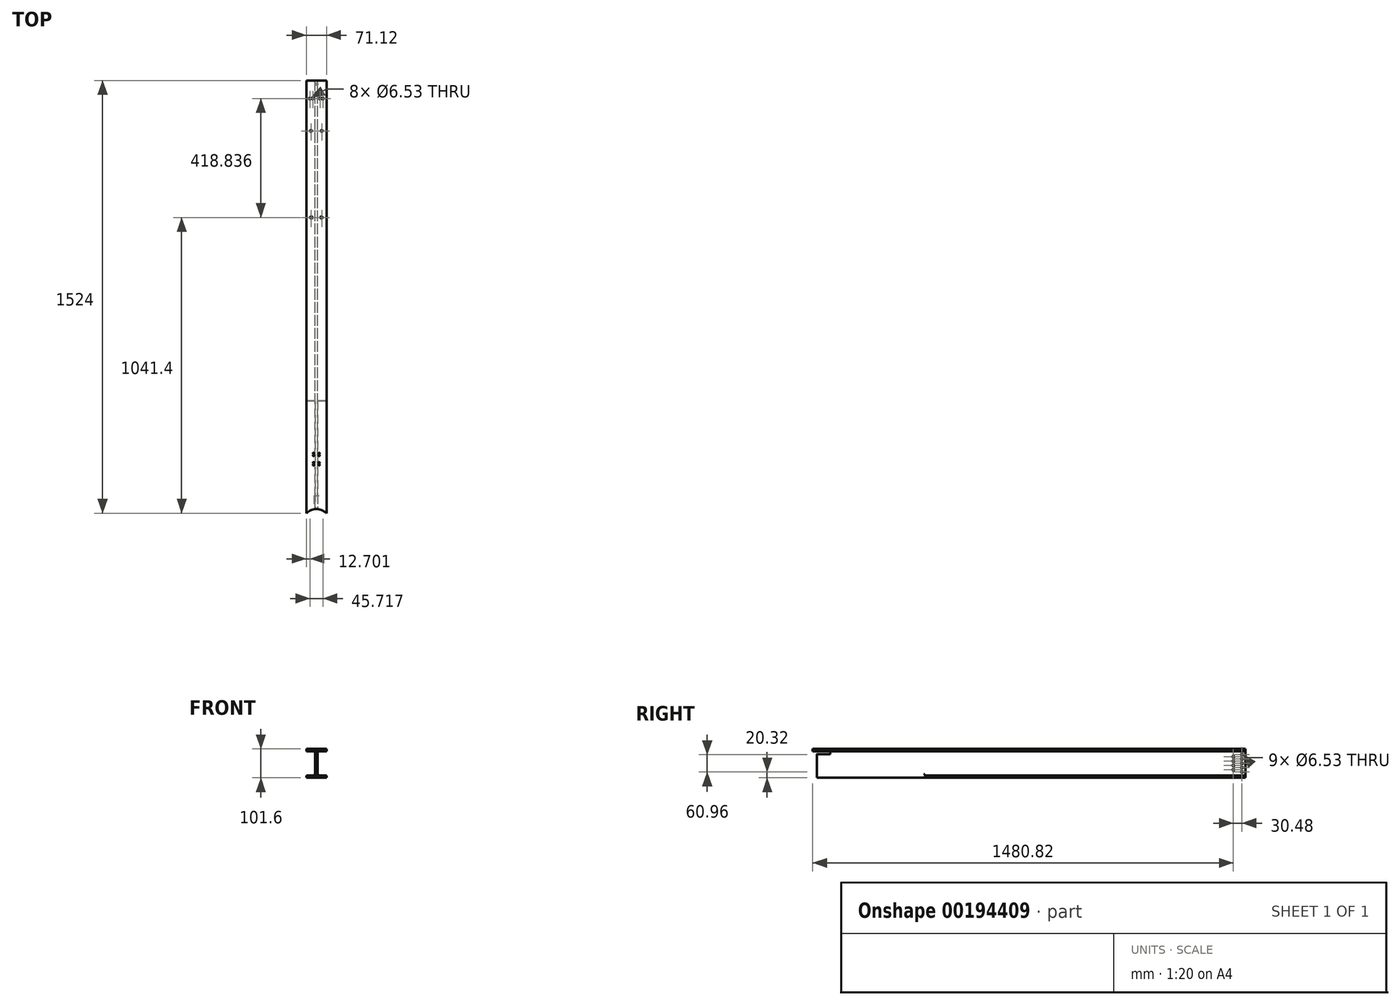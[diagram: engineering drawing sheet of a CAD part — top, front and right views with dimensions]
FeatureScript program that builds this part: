
annotation { "Feature Type Name" : "Feature", "Feature Type Description" : "" }
export const myFeature = defineFeature(function(context is Context, id is Id, definition is map)
    precondition{}
    {
        {
            var Q0;
            Q0=qCreatedBy(makeId("Front.planeOp"),FACE);
            var sketch = newSketch(context, id + "F0", { "sketchPlane" : qUnion([Q0])});
            skLineSegment(sketch, "E0.bottom", {"start": v(35.56, -50.8) * mm, "end": v(-35.56, -50.8) * mm});
            skLineSegment(sketch, "E0.top", {"start": v(35.56, 50.8) * mm, "end": v(-35.56, 50.8) * mm});
            skLineSegment(sketch, "E0.left", {"start": v(35.56, -50.8) * mm, "end": v(35.56, -42.42) * mm});
            skLineSegment(sketch, "E0.right", {"start": v(-35.56, -50.8) * mm, "end": v(-35.56, -42.42) * mm});
            skPoint(sketch, "E0.middle", {"position": v(0, 0) * mm});
            skLineSegment(sketch, "E1", {"start": v(-35.56, 50.8) * mm, "end": v(-35.56, 42.42) * mm});
            skLineSegment(sketch, "E2", {"start": v(-35.56, 42.42) * mm, "end": v(-4.2, 42.42) * mm});
            skLineSegment(sketch, "E3", {"start": v(0, 50.8) * mm, "end": v(-4.2, 50.8) * mm});
            skLineSegment(sketch, "E4", {"start": v(-4.2, 42.42) * mm, "end": v(-4.2, 0) * mm});
            skLineSegment(sketch, "E5.MirrorCS", {"start": v(4.2, 42.42) * mm, "end": v(4.2, 0) * mm});
            skLineSegment(sketch, "E6.MirrorCS", {"start": v(35.56, 50.8) * mm, "end": v(35.56, 42.42) * mm});
            skLineSegment(sketch, "E7.MirrorCS", {"start": v(-35.56, -42.42) * mm, "end": v(-4.2, -42.42) * mm});
            skLineSegment(sketch, "E8.MirrorCS", {"start": v(-4.2, -42.42) * mm, "end": v(-4.2, 0) * mm});
            skLineSegment(sketch, "E9.MirrorCS", {"start": v(4.2, -42.42) * mm, "end": v(4.2, 0) * mm});
            skPoint(sketch, "E10.orphan", {"position": v(0, -50.8) * mm});
            skLineSegment(sketch, "E11.trimOffspring", {"start": v(4.2, -42.42) * mm, "end": v(35.56, -42.42) * mm});
            skLineSegment(sketch, "E12.trimOffspring", {"start": v(4.2, 42.42) * mm, "end": v(35.56, 42.42) * mm});
            skLineSegment(sketch, "E13.trimOffspring", {"start": v(35.56, 42.42) * mm, "end": v(35.56, 50.8) * mm});
            skLineSegment(sketch, "E14.trimOffspring", {"start": v(-35.56, 42.42) * mm, "end": v(-35.56, 50.8) * mm});
            skSolve(sketch);
        }
        {
            var Q0;
            Q0=makeQuery(id+"F0.imprint","IMPRINT",FACE,{"disambiguationData":[TD([[makeQuery(id+"F0.imprint","IMPRINT",EDGE,{"derivedFrom":sQuery(id+"F0.wireOp",EDGE,"E0.bottom")}),-1.0]])]});
            extrude(context, id + "F1", {"entities" : qUnion([Q0]), "depth" : 1524 * mm});
        }
        {
            var Q0;
            Q0=makeQuery(id+"F1.opExtrude","SWEPT_EDGE",EDGE,{"disambiguationData":[OSD([sQuery(id+"F0.wireOp",EDGE,"E5.MirrorCS"),sQuery(id+"F0.wireOp",EDGE,"E12.trimOffspring")])]});
            var Q1;
            Q1=makeQuery(id+"F1.opExtrude","SWEPT_EDGE",EDGE,{"disambiguationData":[OSD([sQuery(id+"F0.wireOp",EDGE,"E9.MirrorCS"),sQuery(id+"F0.wireOp",EDGE,"E11.trimOffspring")])]});
            var Q2;
            Q2=makeQuery(id+"F1.opExtrude","SWEPT_EDGE",EDGE,{"disambiguationData":[OSD([sQuery(id+"F0.wireOp",EDGE,"E7.MirrorCS"),sQuery(id+"F0.wireOp",EDGE,"E8.MirrorCS")])]});
            var Q3;
            Q3=makeQuery(id+"F1.opExtrude","SWEPT_EDGE",EDGE,{"disambiguationData":[OSD([sQuery(id+"F0.wireOp",EDGE,"E2"),sQuery(id+"F0.wireOp",EDGE,"E4")])]});
            fillet(context, id + "F2", {"entities" : qUnion([Q0, Q1, Q2, Q3]), "radius" : 5.08 * mm, "tangentPropagation" : true, "allowEdgeOverflow" : false});
        }
        {
            var Q0;
            Q0=makeQuery(id+"F1.opExtrude","SWEPT_FACE",FACE,{"disambiguationData":[OSD([sQuery(id+"F0.wireOp",EDGE,"E0.top"),sQuery(id+"F0.wireOp",EDGE,"E3")])]});
            var sketch = newSketch(context, id + "F3", { "sketchPlane" : qUnion([Q0])});
            skLineSegment(sketch, "E15", {"start": v(0, -1524) * mm, "end": v(0, -1560.28) * mm});
            skPoint(sketch, "E15.endSnap0", {"position": v(0, -1524) * mm});
            skLineSegment(sketch, "E16", {"start": v(35.56, -1524) * mm, "end": v(0, -1560.28) * mm});
            skCircle(sketch, "E17", {"center": v(0, -1560.28) * mm, "radius": 50.8 * mm});
            skLineSegment(sketch, "E18.trimOffspring", {"start": v(0, -1611.08) * mm, "end": v(0, -1676.71) * mm});
            skSolve(sketch);
        }
        {
            var Q0;
            {var subQ6=sQuery(id+"F3.wireOp",EDGE,"E15");Q0=makeQuery(id+"F3.imprint","IMPRINT",FACE,{"disambiguationData":[TD([[makeQuery(id+"F3.imprint","IMPRINT",EDGE,{"derivedFrom":subQ6}),-1.0]])]});}
            var Q1;
            {var subQ0=sQuery(id+"F3.wireOp",EDGE,"E15");Q1=makeQuery(id+"F3.imprint","IMPRINT",FACE,{"disambiguationData":[TD([[makeQuery(id+"F3.imprint","IMPRINT",EDGE,{"derivedFrom":subQ0}),1.0]])]});}
            var Q2;
            {var subQ1=sQuery(id+"F0.wireOp",EDGE,"E0.top");var subQ2=makeQuery(id+"F1.opExtrude","CAP_EDGE",EDGE,{"disambiguationData":[OSD([subQ1,sQuery(id+"F0.wireOp",EDGE,"E3")])],"isStart":false});var subQ5=makeQuery(id+"F3.imprint","INTERSECT",VERTEX,{"derivedFrom":[subQ2,sQuery(id+"F3.wireOp",EDGE,"E15")]});Q2=makeQuery(id+"F3.imprint","IMPRINT",FACE,{"disambiguationData":[TD([[makeQuery(id+"F3.imprint","IMPRINT",EDGE,{"disambiguationData":[TD([[subQ5,-1.0]])],"derivedFrom":subQ2}),-1.0]])]});}
            extrude(context, id + "F4", {"entities" : qUnion([Q0, Q1, Q2]), "operationType" : NewBodyOperationType.REMOVE, "oppositeDirection" : true, "depth" : 101.6 * mm});
        }
        {
            var Q0;
            Q0=makeQuery(id+"F1.opExtrude","SWEPT_FACE",FACE,{"disambiguationData":[OSD([sQuery(id+"F0.wireOp",EDGE,"E5.MirrorCS"),sQuery(id+"F0.wireOp",EDGE,"E9.MirrorCS")])]});
            var sketch = newSketch(context, id + "F5", { "sketchPlane" : qUnion([Q0])});
            skSolve(sketch);
        }
        {
            var Q0;
            {var subQ0=sQuery(id+"F0.wireOp",EDGE,"E9.MirrorCS");var subQ1=sQuery(id+"F0.wireOp",EDGE,"E5.MirrorCS");Q0=makeQuery(id+"F5.imprint","IMPRINT",FACE,{"disambiguationData":[TD([[makeQuery(id+"F5.imprint","IMPRINT",EDGE,{"derivedFrom":makeQuery(id+"F1.opExtrude","CAP_EDGE",EDGE,{"disambiguationData":[OSD([subQ1,subQ0])],"isStart":true})}),1.0]])]});}
            var sketch = newSketch(context, id + "F6", { "sketchPlane" : qUnion([Q0])});
            skLineSegment(sketch, "E19", {"start": v(-1510.33, 42.42) * mm, "end": v(-1510.33, 32.26) * mm});
            skLineSegment(sketch, "E20", {"start": v(-1510.33, 32.26) * mm, "end": v(-1462.07, 32.26) * mm});
            skLineSegment(sketch, "E21", {"start": v(-1462.07, 32.26) * mm, "end": v(-1462.07, 42.42) * mm});
            skLineSegment(sketch, "E22", {"start": v(-1462.07, 42.42) * mm, "end": v(-1510.33, 42.42) * mm});
            skSolve(sketch);
        }
        {
            var Q0;
            Q0 = qSketchRegion(id + "F6", true);
            extrude(context, id + "F7", {"entities" : qUnion([Q0]), "operationType" : NewBodyOperationType.REMOVE, "endBound" : BoundingType.SYMMETRIC, "oppositeDirection" : true, "depth" : 25.4 * mm});
        }
        {
            var Q0;
            Q0=makeQuery(id+"F7.boolean.opBoolean","INTERSECT",EDGE,{"derivedFrom":[makeQuery(id+"F4.boolean.opBoolean","COPY",FACE,{"derivedFrom":makeQuery(id+"F4.opExtrude","SWEPT_FACE",FACE,{"disambiguationData":[OSD([sQuery(id+"F3.wireOp",EDGE,"E17")])]})}),makeQuery(id+"F7.opExtrude","SWEPT_FACE",FACE,{"disambiguationData":[OSD([sQuery(id+"F6.wireOp",EDGE,"E20")])]})]});
            chamfer(context, id + "F8", {"entities" : qUnion([Q0]), "width" : 1.27 * mm, "tangentPropagation" : true});
        }
        {
            var Q0;
            Q0=makeQuery(id+"F1.opExtrude","SWEPT_FACE",FACE,{"disambiguationData":[OSD([sQuery(id+"F0.wireOp",EDGE,"E0.top"),sQuery(id+"F0.wireOp",EDGE,"E3")])]});
            var sketch = newSketch(context, id + "F9", { "sketchPlane" : qUnion([Q0])});
            skLineSegment(sketch, "E23", {"start": v(-0.26, -1524) * mm, "end": v(-0.26, -0.03) * mm});
            skLineSegment(sketch, "E24.bottom", {"start": v(9.71, -1353.82) * mm, "end": v(-10.23, -1353.82) * mm});
            skLineSegment(sketch, "E24.top", {"start": v(9.71, -1313.18) * mm, "end": v(-10.23, -1313.18) * mm});
            skLineSegment(sketch, "E25.bottom", {"start": v(9.71, -1346.2) * mm, "end": v(-10.23, -1346.2) * mm});
            skLineSegment(sketch, "E25.top", {"start": v(9.71, -1320.8) * mm, "end": v(-10.23, -1320.8) * mm});
            skLineSegment(sketch, "E26", {"start": v(35.56, -1524) * mm, "end": v(-35.56, -1524) * mm});
            skLineSegment(sketch, "E27", {"start": v(-0.26, -1524) * mm, "end": v(-0.26, -1353.82) * mm});
            skLineSegment(sketch, "E28", {"start": v(-0.26, -1353.82) * mm, "end": v(-0.26, -1346.2) * mm});
            skLineSegment(sketch, "E29", {"start": v(-0.26, -1346.2) * mm, "end": v(-0.26, -1320.8) * mm});
            skLineSegment(sketch, "E30", {"start": v(-0.26, -1320.8) * mm, "end": v(-0.26, -1313.18) * mm});
            skSolve(sketch);
        }
        {
            var Q0;
            Q0=sQuery(id+"F9.wireOp",VERTEX,"E24.bottom.end");
            var Q1;
            Q1=sQuery(id+"F9.wireOp",VERTEX,"E25.bottom.end");
            var Q2;
            Q2=sQuery(id+"F9.wireOp",VERTEX,"E25.top.end");
            var Q3;
            Q3=sQuery(id+"F9.wireOp",VERTEX,"E24.top.end");
            var Q4;
            Q4=sQuery(id+"F9.wireOp",VERTEX,"E24.top.start");
            var Q5;
            Q5=sQuery(id+"F9.wireOp",VERTEX,"E25.top.start");
            var Q6;
            Q6=sQuery(id+"F9.wireOp",VERTEX,"E25.bottom.start");
            var Q7;
            Q7=sQuery(id+"F9.wireOp",VERTEX,"E24.bottom.start");
            var Q8;
            Q8=makeQuery(id+"F1.opExtrude","SWEPT_BODY",BODY,{"disambiguationData":[OSD([sQuery(id+"F0.wireOp",EDGE,"E0.bottom"),sQuery(id+"F0.wireOp",EDGE,"E0.top"),sQuery(id+"F0.wireOp",EDGE,"E0.left"),sQuery(id+"F0.wireOp",EDGE,"E0.right"),sQuery(id+"F0.wireOp",EDGE,"E2"),sQuery(id+"F0.wireOp",EDGE,"E3"),sQuery(id+"F0.wireOp",EDGE,"E4"),sQuery(id+"F0.wireOp",EDGE,"E5.MirrorCS"),sQuery(id+"F0.wireOp",EDGE,"E7.MirrorCS"),sQuery(id+"F0.wireOp",EDGE,"E8.MirrorCS"),sQuery(id+"F0.wireOp",EDGE,"E9.MirrorCS"),sQuery(id+"F0.wireOp",EDGE,"E11.trimOffspring"),sQuery(id+"F0.wireOp",EDGE,"E12.trimOffspring"),sQuery(id+"F0.wireOp",EDGE,"E13.trimOffspring"),sQuery(id+"F0.wireOp",EDGE,"E14.trimOffspring")])]});
            hole(context, id + "F10", {"style" : HoleStyle.SIMPLE, "endStyle" : HoleEndStyle.BLIND, "standardTappedOrClearance" : lookupTablePath({ "standard" : "ANSI", "fit" : "Close", "size" : "#8", "type" : "Clearance" }), "standardBlindInLast" : lookupTablePath({ "fit" : "Close", "standard" : "ANSI", "size" : "#8", "type" : "Clearance" }), "holeDiameter" : 4.32 * mm, "holeDepth" : 25.4 * mm, "locations" : qUnion([Q0, Q1, Q2, Q3, Q4, Q5, Q6, Q7]), "scope" : qUnion([Q8])});
        }
        {
            var Q0;
            Q0=makeQuery(id+"F1.opExtrude","SWEPT_FACE",FACE,{"disambiguationData":[OSD([sQuery(id+"F0.wireOp",EDGE,"E0.bottom")])]});
            var sketch = newSketch(context, id + "F11", { "sketchPlane" : qUnion([Q0])});
            skLineSegment(sketch, "E31", {"start": v(4.2, 1509.65) * mm, "end": v(4.2, 1128.65) * mm});
            skLineSegment(sketch, "E32.bottom", {"start": v(4.2, 1128.65) * mm, "end": v(39.68, 1128.65) * mm});
            skLineSegment(sketch, "E32.top", {"start": v(4.2, 1528.41) * mm, "end": v(39.68, 1528.41) * mm});
            skLineSegment(sketch, "E32.left", {"start": v(4.2, 1128.65) * mm, "end": v(4.2, 1528.41) * mm});
            skLineSegment(sketch, "E32.right", {"start": v(39.68, 1128.65) * mm, "end": v(39.68, 1528.41) * mm});
            skLineSegment(sketch, "E33", {"start": v(0, 1526.52) * mm, "end": v(0, 1517.43) * mm});
            skLineSegment(sketch, "E34.MirrorCS", {"start": v(-4.2, 1528.41) * mm, "end": v(-39.68, 1528.41) * mm});
            skLineSegment(sketch, "E35.MirrorCS", {"start": v(-39.68, 1128.65) * mm, "end": v(-39.68, 1528.41) * mm});
            skLineSegment(sketch, "E36.MirrorCS", {"start": v(-4.2, 1128.65) * mm, "end": v(-4.2, 1528.41) * mm});
            skLineSegment(sketch, "E37.MirrorCS", {"start": v(-4.2, 1128.65) * mm, "end": v(-39.68, 1128.65) * mm});
            skSolve(sketch);
        }
        {
            var Q0;
            Q0 = qSketchRegion(id + "F11", true);
            extrude(context, id + "F12", {"entities" : qUnion([Q0]), "operationType" : NewBodyOperationType.REMOVE, "oppositeDirection" : true, "depth" : 25.4 * mm});
        }
        {
            var Q0;
            Q0=makeQuery(id+"F12.boolean.opBoolean","COPY",EDGE,{"derivedFrom":makeQuery(id+"F12.opExtrude","SWEPT_EDGE",EDGE,{"disambiguationData":[OSD([sQuery(id+"F11.wireOp",EDGE,"E32.bottom"),sQuery(id+"F11.wireOp",EDGE,"E32.left")])]})});
            var Q1;
            Q1=makeQuery(id+"F12.boolean.opBoolean","COPY",EDGE,{"derivedFrom":makeQuery(id+"F12.opExtrude","SWEPT_EDGE",EDGE,{"disambiguationData":[OSD([sQuery(id+"F11.wireOp",EDGE,"E36.MirrorCS"),sQuery(id+"F11.wireOp",EDGE,"E37.MirrorCS")])]})});
            fillet(context, id + "F13", {"entities" : qUnion([Q0, Q1]), "radius" : 3.17 * mm, "tangentPropagation" : true, "allowEdgeOverflow" : false});
        }
        {
            var Q0;
            {var subQ0=sQuery(id+"F0.wireOp",EDGE,"E9.MirrorCS");var subQ1=sQuery(id+"F0.wireOp",EDGE,"E5.MirrorCS");Q0=makeQuery(id+"F5.imprint","IMPRINT",FACE,{"disambiguationData":[TD([[makeQuery(id+"F5.imprint","IMPRINT",EDGE,{"derivedFrom":makeQuery(id+"F1.opExtrude","CAP_EDGE",EDGE,{"disambiguationData":[OSD([subQ1,subQ0])],"isStart":true})}),1.0]])]});}
            var sketch = newSketch(context, id + "F14", { "sketchPlane" : qUnion([Q0])});
            skLineSegment(sketch, "E38", {"start": v(0, 37.34) * mm, "end": v(0, -37.34) * mm});
            skLineSegment(sketch, "E39", {"start": v(0, 0) * mm, "end": v(-30.48, 0) * mm});
            skLineSegment(sketch, "E40.bottom", {"start": v(-12.7, 30.48) * mm, "end": v(-48.26, 30.48) * mm});
            skLineSegment(sketch, "E40.top", {"start": v(-12.7, -30.48) * mm, "end": v(-48.26, -30.48) * mm});
            skLineSegment(sketch, "E40.left", {"start": v(-12.7, 30.48) * mm, "end": v(-12.7, -30.48) * mm});
            skLineSegment(sketch, "E40.right", {"start": v(-48.26, 30.48) * mm, "end": v(-48.26, -30.48) * mm});
            skPoint(sketch, "E40.middle", {"position": v(-30.48, 0) * mm});
            skLineSegment(sketch, "E41", {"start": v(-12.7, -30.48) * mm, "end": v(-12.7, -15.24) * mm});
            skLineSegment(sketch, "E42", {"start": v(-12.7, -15.24) * mm, "end": v(-12.7, 0) * mm});
            skLineSegment(sketch, "E43", {"start": v(-12.7, 0) * mm, "end": v(-12.7, 15.24) * mm});
            skLineSegment(sketch, "E44", {"start": v(-12.7, 15.24) * mm, "end": v(-12.7, 30.48) * mm});
            skLineSegment(sketch, "E45", {"start": v(-12.7, 30.48) * mm, "end": v(-43.18, 30.48) * mm});
            skLineSegment(sketch, "E46", {"start": v(-43.18, 30.48) * mm, "end": v(-43.18, 22.86) * mm});
            skLineSegment(sketch, "E47", {"start": v(-43.18, 22.86) * mm, "end": v(-43.18, 7.62) * mm});
            skLineSegment(sketch, "E48", {"start": v(-43.18, 7.62) * mm, "end": v(-43.18, -7.62) * mm});
            skLineSegment(sketch, "E49", {"start": v(-43.18, -7.62) * mm, "end": v(-43.18, -22.86) * mm});
            skSolve(sketch);
        }
        {
            var Q0;
            Q0=sQuery(id+"F14.wireOp",VERTEX,"E46.end");
            var Q1;
            Q1=sQuery(id+"F14.wireOp",VERTEX,"E47.end");
            var Q2;
            Q2=sQuery(id+"F14.wireOp",VERTEX,"E44.end");
            var Q3;
            Q3=sQuery(id+"F14.wireOp",VERTEX,"E43.end");
            var Q4;
            Q4=sQuery(id+"F14.wireOp",VERTEX,"E42.end");
            var Q5;
            Q5=sQuery(id+"F14.wireOp",VERTEX,"E41.end");
            var Q6;
            Q6=sQuery(id+"F14.wireOp",VERTEX,"E40.left.end");
            var Q7;
            Q7=sQuery(id+"F14.wireOp",VERTEX,"E49.start");
            var Q8;
            Q8=sQuery(id+"F14.wireOp",VERTEX,"E49.end");
            var Q9;
            Q9=makeQuery(id+"F1.opExtrude","SWEPT_BODY",BODY,{"disambiguationData":[OSD([sQuery(id+"F0.wireOp",EDGE,"E0.bottom"),sQuery(id+"F0.wireOp",EDGE,"E0.top"),sQuery(id+"F0.wireOp",EDGE,"E0.left"),sQuery(id+"F0.wireOp",EDGE,"E0.right"),sQuery(id+"F0.wireOp",EDGE,"E2"),sQuery(id+"F0.wireOp",EDGE,"E3"),sQuery(id+"F0.wireOp",EDGE,"E4"),sQuery(id+"F0.wireOp",EDGE,"E5.MirrorCS"),sQuery(id+"F0.wireOp",EDGE,"E7.MirrorCS"),sQuery(id+"F0.wireOp",EDGE,"E8.MirrorCS"),sQuery(id+"F0.wireOp",EDGE,"E9.MirrorCS"),sQuery(id+"F0.wireOp",EDGE,"E11.trimOffspring"),sQuery(id+"F0.wireOp",EDGE,"E12.trimOffspring"),sQuery(id+"F0.wireOp",EDGE,"E13.trimOffspring"),sQuery(id+"F0.wireOp",EDGE,"E14.trimOffspring")])]});
            hole(context, id + "F15", {"style" : HoleStyle.SIMPLE, "endStyle" : HoleEndStyle.BLIND, "standardTappedOrClearance" : lookupTablePath({ "standard" : "ANSI", "fit" : "Close", "size" : "1/4", "type" : "Clearance" }), "standardBlindInLast" : lookupTablePath({ "fit" : "Close", "standard" : "ANSI", "size" : "1/4", "type" : "Clearance" }), "holeDiameter" : 6.53 * mm, "holeDepth" : 25.4 * mm, "locations" : qUnion([Q0, Q1, Q2, Q3, Q4, Q5, Q6, Q7, Q8]), "scope" : qUnion([Q9])});
        }
        {
            var Q0;
            Q0=makeQuery(id+"F1.opExtrude","SWEPT_FACE",FACE,{"disambiguationData":[OSD([sQuery(id+"F0.wireOp",EDGE,"E0.top"),sQuery(id+"F0.wireOp",EDGE,"E3")])]});
            var sketch = newSketch(context, id + "F16", { "sketchPlane" : qUnion([Q0])});
            skLineSegment(sketch, "E50", {"start": v(0, 0) * mm, "end": v(0, -63.76) * mm});
            skPoint(sketch, "E50.endSnap0", {"position": v(0, 0) * mm});
            skLineSegment(sketch, "E51", {"start": v(0, -63.76) * mm, "end": v(12.7, -63.76) * mm});
            skLineSegment(sketch, "E52", {"start": v(12.7, -63.76) * mm, "end": v(22.86, -63.94) * mm});
            skLineSegment(sketch, "E53.MirrorCS", {"start": v(0, -63.76) * mm, "end": v(-12.7, -63.76) * mm});
            skLineSegment(sketch, "E54.MirrorCS", {"start": v(-12.7, -63.76) * mm, "end": v(-22.86, -63.94) * mm});
            skSolve(sketch);
        }
        {
            var Q0;
            Q0=sQuery(id+"F16.wireOp",VERTEX,"E54.MirrorCS.end");
            var Q1;
            Q1=sQuery(id+"F16.wireOp",VERTEX,"E53.MirrorCS.end");
            var Q2;
            Q2=sQuery(id+"F16.wireOp",VERTEX,"E51.end");
            var Q3;
            Q3=sQuery(id+"F16.wireOp",VERTEX,"E52.end");
            var Q4;
            Q4=makeQuery(id+"F1.opExtrude","SWEPT_BODY",BODY,{"disambiguationData":[OSD([sQuery(id+"F0.wireOp",EDGE,"E0.bottom"),sQuery(id+"F0.wireOp",EDGE,"E0.top"),sQuery(id+"F0.wireOp",EDGE,"E0.left"),sQuery(id+"F0.wireOp",EDGE,"E0.right"),sQuery(id+"F0.wireOp",EDGE,"E2"),sQuery(id+"F0.wireOp",EDGE,"E3"),sQuery(id+"F0.wireOp",EDGE,"E4"),sQuery(id+"F0.wireOp",EDGE,"E5.MirrorCS"),sQuery(id+"F0.wireOp",EDGE,"E7.MirrorCS"),sQuery(id+"F0.wireOp",EDGE,"E8.MirrorCS"),sQuery(id+"F0.wireOp",EDGE,"E9.MirrorCS"),sQuery(id+"F0.wireOp",EDGE,"E11.trimOffspring"),sQuery(id+"F0.wireOp",EDGE,"E12.trimOffspring"),sQuery(id+"F0.wireOp",EDGE,"E13.trimOffspring"),sQuery(id+"F0.wireOp",EDGE,"E14.trimOffspring")])]});
            hole(context, id + "F17", {"style" : HoleStyle.SIMPLE, "endStyle" : HoleEndStyle.BLIND, "standardTappedOrClearance" : lookupTablePath({ "standard" : "ANSI", "fit" : "Close", "size" : "1/4", "type" : "Clearance" }), "standardBlindInLast" : lookupTablePath({ "fit" : "Close", "standard" : "ANSI", "size" : "1/4", "type" : "Clearance" }), "holeDiameter" : 6.53 * mm, "holeDepth" : 25.4 * mm, "locations" : qUnion([Q0, Q1, Q2, Q3]), "scope" : qUnion([Q4])});
        }
        {
            var Q0;
            Q0=makeQuery(id+"F1.opExtrude","SWEPT_FACE",FACE,{"disambiguationData":[OSD([sQuery(id+"F0.wireOp",EDGE,"E0.top"),sQuery(id+"F0.wireOp",EDGE,"E3")])]});
            var sketch = newSketch(context, id + "F18", { "sketchPlane" : qUnion([Q0])});
            skLineSegment(sketch, "E55", {"start": v(0, 0) * mm, "end": v(0, -177.8) * mm});
            skPoint(sketch, "E55.endSnap0", {"position": v(0, 0) * mm});
            skLineSegment(sketch, "E56", {"start": v(0, -177.8) * mm, "end": v(-19.05, -177.8) * mm});
            skLineSegment(sketch, "E57", {"start": v(-19.05, -177.8) * mm, "end": v(19.05, -177.8) * mm});
            skLineSegment(sketch, "E58", {"start": v(19.05, -177.8) * mm, "end": v(0, -177.8) * mm});
            skLineSegment(sketch, "E59", {"start": v(0, -177.8) * mm, "end": v(0, -482.6) * mm});
            skLineSegment(sketch, "E60", {"start": v(0, -482.6) * mm, "end": v(-19.05, -482.6) * mm});
            skLineSegment(sketch, "E61", {"start": v(-19.05, -482.6) * mm, "end": v(19.05, -482.6) * mm});
            skSolve(sketch);
        }
        {
            var Q0;
            Q0=sQuery(id+"F18.wireOp",VERTEX,"E57.end");
            var Q1;
            Q1=sQuery(id+"F18.wireOp",VERTEX,"E56.end");
            var Q2;
            Q2=sQuery(id+"F18.wireOp",VERTEX,"E61.start");
            var Q3;
            Q3=sQuery(id+"F18.wireOp",VERTEX,"E61.end");
            var Q4;
            Q4=makeQuery(id+"F1.opExtrude","SWEPT_BODY",BODY,{"disambiguationData":[OSD([sQuery(id+"F0.wireOp",EDGE,"E0.bottom"),sQuery(id+"F0.wireOp",EDGE,"E0.top"),sQuery(id+"F0.wireOp",EDGE,"E0.left"),sQuery(id+"F0.wireOp",EDGE,"E0.right"),sQuery(id+"F0.wireOp",EDGE,"E2"),sQuery(id+"F0.wireOp",EDGE,"E3"),sQuery(id+"F0.wireOp",EDGE,"E4"),sQuery(id+"F0.wireOp",EDGE,"E5.MirrorCS"),sQuery(id+"F0.wireOp",EDGE,"E7.MirrorCS"),sQuery(id+"F0.wireOp",EDGE,"E8.MirrorCS"),sQuery(id+"F0.wireOp",EDGE,"E9.MirrorCS"),sQuery(id+"F0.wireOp",EDGE,"E11.trimOffspring"),sQuery(id+"F0.wireOp",EDGE,"E12.trimOffspring"),sQuery(id+"F0.wireOp",EDGE,"E13.trimOffspring"),sQuery(id+"F0.wireOp",EDGE,"E14.trimOffspring")])]});
            hole(context, id + "F19", {"style" : HoleStyle.SIMPLE, "endStyle" : HoleEndStyle.BLIND, "standardTappedOrClearance" : lookupTablePath({ "standard" : "ANSI", "fit" : "Close", "size" : "1/4", "type" : "Clearance" }), "standardBlindInLast" : lookupTablePath({ "fit" : "Close", "standard" : "ANSI", "size" : "1/4", "type" : "Clearance" }), "holeDiameter" : 6.53 * mm, "holeDepth" : 25.4 * mm, "locations" : qUnion([Q0, Q1, Q2, Q3]), "scope" : qUnion([Q4])});
        }
        {
            var Q0;
            Q0=makeQuery(id+"F1.opExtrude","SWEPT_FACE",FACE,{"disambiguationData":[OSD([sQuery(id+"F0.wireOp",EDGE,"E0.bottom")])]});
            var sketch = newSketch(context, id + "F20", { "sketchPlane" : qUnion([Q0])});
            skLineSegment(sketch, "E62", {"start": v(0, 0) * mm, "end": v(0, 482.6) * mm});
            skPoint(sketch, "E62.endSnap0", {"position": v(0, 0) * mm});
            skLineSegment(sketch, "E63", {"start": v(0, 482.6) * mm, "end": v(15.88, 482.6) * mm});
            skLineSegment(sketch, "E64", {"start": v(15.88, 482.6) * mm, "end": v(-15.88, 482.6) * mm});
            skSolve(sketch);
        }
        {
            var Q0;
            Q0=sQuery(id+"F20.wireOp",VERTEX,"E64.start");
            var Q1;
            Q1=sQuery(id+"F20.wireOp",VERTEX,"E64.end");
            var Q2;
            Q2=makeQuery(id+"F1.opExtrude","SWEPT_BODY",BODY,{"disambiguationData":[OSD([sQuery(id+"F0.wireOp",EDGE,"E0.bottom"),sQuery(id+"F0.wireOp",EDGE,"E0.top"),sQuery(id+"F0.wireOp",EDGE,"E0.left"),sQuery(id+"F0.wireOp",EDGE,"E0.right"),sQuery(id+"F0.wireOp",EDGE,"E2"),sQuery(id+"F0.wireOp",EDGE,"E3"),sQuery(id+"F0.wireOp",EDGE,"E4"),sQuery(id+"F0.wireOp",EDGE,"E5.MirrorCS"),sQuery(id+"F0.wireOp",EDGE,"E7.MirrorCS"),sQuery(id+"F0.wireOp",EDGE,"E8.MirrorCS"),sQuery(id+"F0.wireOp",EDGE,"E9.MirrorCS"),sQuery(id+"F0.wireOp",EDGE,"E11.trimOffspring"),sQuery(id+"F0.wireOp",EDGE,"E12.trimOffspring"),sQuery(id+"F0.wireOp",EDGE,"E13.trimOffspring"),sQuery(id+"F0.wireOp",EDGE,"E14.trimOffspring")])]});
            hole(context, id + "F21", {"style" : HoleStyle.SIMPLE, "endStyle" : HoleEndStyle.BLIND, "standardTappedOrClearance" : lookupTablePath({ "standard" : "ANSI", "fit" : "Close", "size" : "3/8", "type" : "Clearance" }), "standardBlindInLast" : lookupTablePath({ "fit" : "Close", "standard" : "ANSI", "size" : "3/8", "type" : "Clearance" }), "holeDiameter" : 9.8 * mm, "holeDepth" : 25.4 * mm, "locations" : qUnion([Q0, Q1]), "scope" : qUnion([Q2])});
        }
    });
